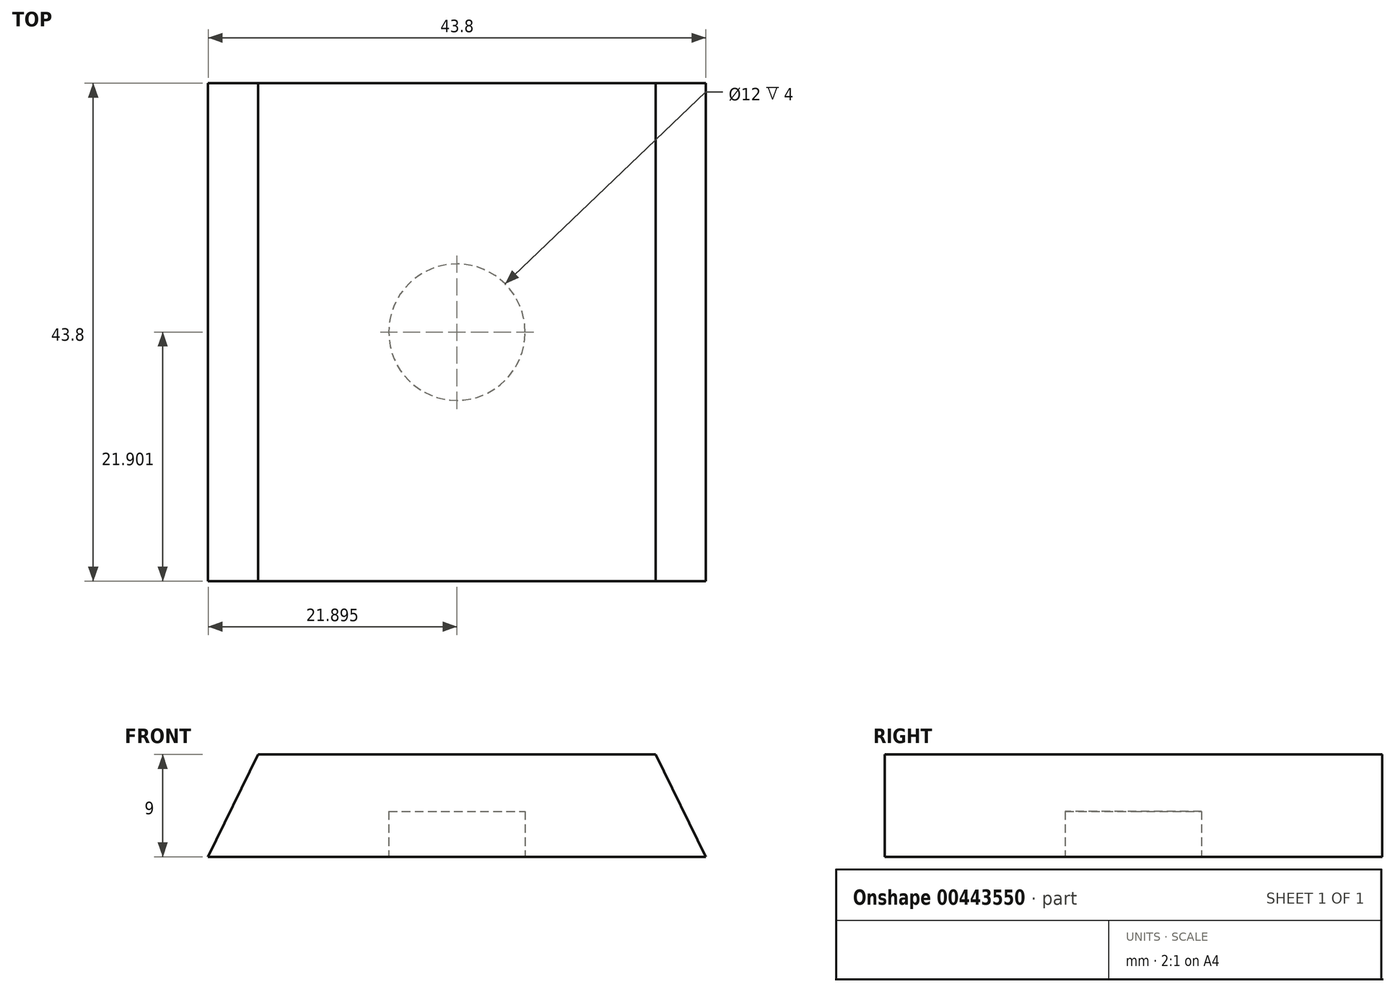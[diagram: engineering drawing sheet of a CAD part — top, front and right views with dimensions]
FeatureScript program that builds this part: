
annotation { "Feature Type Name" : "Feature", "Feature Type Description" : "" }
export const myFeature = defineFeature(function(context is Context, id is Id, definition is map)
    precondition{}
    {
        {
            var Q0;
            Q0=qCreatedBy(makeId("Top.planeOp"),FACE);
            var sketch = newSketch(context, id + "F0", { "sketchPlane" : qUnion([Q0])});
            skLineSegment(sketch, "E0.bottom", {"start": v(-15.61, 22.47) * mm, "end": v(28.19, 22.47) * mm});
            skLineSegment(sketch, "E0.top", {"start": v(-15.61, -21.33) * mm, "end": v(28.19, -21.33) * mm});
            skLineSegment(sketch, "E0.left", {"start": v(-15.61, 22.47) * mm, "end": v(-15.61, -21.33) * mm});
            skLineSegment(sketch, "E0.right", {"start": v(28.19, 22.47) * mm, "end": v(28.19, -21.33) * mm});
            skSolve(sketch);
        }
        {
            var Q0;
            Q0 = qSketchRegion(id + "F0", true);
            extrude(context, id + "F1", {"entities" : qUnion([Q0]), "depth" : 9 * mm});
        }
        {
            var Q0;
            Q0=makeQuery(id+"F1.opExtrude","SWEPT_FACE",FACE,{"disambiguationData":[OSD([sQuery(id+"F0.wireOp",EDGE,"E0.top")])]});
            var sketch = newSketch(context, id + "F2", { "sketchPlane" : qUnion([Q0])});
            skLineSegment(sketch, "E1", {"start": v(-11.21, 9) * mm, "end": v(23.79, 9) * mm});
            skLineSegment(sketch, "E2", {"start": v(-11.21, 9) * mm, "end": v(-15.61, 0) * mm});
            skLineSegment(sketch, "E3", {"start": v(-15.61, 0) * mm, "end": v(28.19, 0) * mm});
            skLineSegment(sketch, "E4", {"start": v(28.19, 0) * mm, "end": v(23.79, 9) * mm});
            skLineSegment(sketch, "E5", {"start": v(-11.21, 9) * mm, "end": v(-15.61, 9) * mm});
            skLineSegment(sketch, "E6", {"start": v(-15.61, 9) * mm, "end": v(-15.61, 0) * mm});
            skLineSegment(sketch, "E7", {"start": v(23.79, 9) * mm, "end": v(28.19, 9) * mm});
            skLineSegment(sketch, "E8", {"start": v(28.19, 9) * mm, "end": v(28.19, 0) * mm});
            skSolve(sketch);
        }
        {
            var Q0;
            Q0=makeQuery(id+"F2.imprint","IMPRINT",FACE,{"disambiguationData":[TD([[makeQuery(id+"F2.imprint","IMPRINT",EDGE,{"derivedFrom":sQuery(id+"F2.wireOp",EDGE,"E2")}),-1.0]])]});
            var Q1;
            Q1=makeQuery(id+"F2.imprint","IMPRINT",FACE,{"disambiguationData":[TD([[makeQuery(id+"F2.imprint","IMPRINT",EDGE,{"derivedFrom":sQuery(id+"F2.wireOp",EDGE,"E4")}),-1.0]])]});
            var Q2;
            Q2=makeQuery(id+"F1.opExtrude","SWEPT_FACE",FACE,{"disambiguationData":[OSD([sQuery(id+"F0.wireOp",EDGE,"E0.bottom")])]});
            extrude(context, id + "F3", {"entities" : qUnion([Q0, Q1]), "operationType" : NewBodyOperationType.REMOVE, "endBound" : BoundingType.UP_TO_SURFACE, "oppositeDirection" : true, "endBoundEntityFace" : qUnion([Q2]), "depth" : 25 * mm});
        }
        {
            var Q0;
            Q0=makeQuery(id+"F1.opExtrude","CAP_FACE",FACE,{"disambiguationData":[OSD([sQuery(id+"F0.wireOp",EDGE,"E0.bottom"),sQuery(id+"F0.wireOp",EDGE,"E0.top"),sQuery(id+"F0.wireOp",EDGE,"E0.left"),sQuery(id+"F0.wireOp",EDGE,"E0.right")])],"isStart":true});
            var sketch = newSketch(context, id + "F4", { "sketchPlane" : qUnion([Q0])});
            skCircle(sketch, "E9", {"center": v(6.29, -0.57) * mm, "radius": 6 * mm});
            skLineSegment(sketch, "E10", {"start": v(28.19, 21.33) * mm, "end": v(-15.61, -22.47) * mm});
            skLineSegment(sketch, "E11", {"start": v(28.19, -22.47) * mm, "end": v(-15.61, 21.33) * mm});
            skSolve(sketch);
        }
        {
            var Q0;
            Q0 = qSketchRegion(id + "F4", true);
            extrude(context, id + "F5", {"entities" : qUnion([Q0]), "operationType" : NewBodyOperationType.REMOVE, "oppositeDirection" : true, "depth" : 4 * mm});
        }
    });
